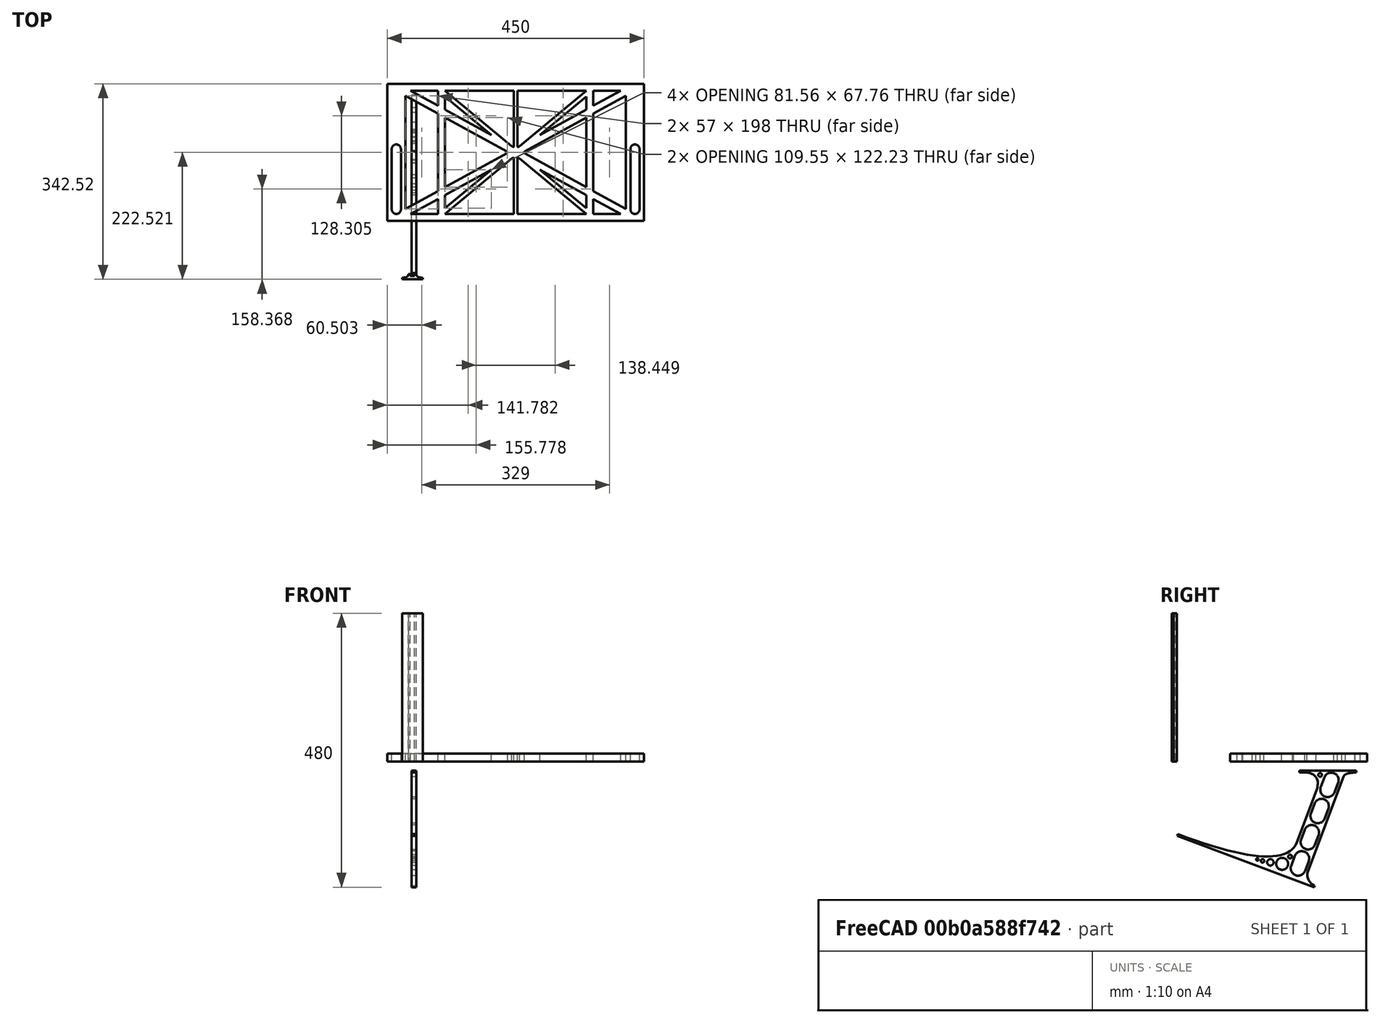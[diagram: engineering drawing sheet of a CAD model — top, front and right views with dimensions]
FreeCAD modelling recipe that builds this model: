
FCSTD DOCUMENT  (FreeCAD 0.19R0.19.2)
Label: laptopStand061
License: All rights reserved
LicenseURL: http://en.wikipedia.org/wiki/All_rights_reserved
objects: Sketcher::SketchObject×3, Part::Extrusion×3
note: 6 computed .brp shape members not serialized (recipe doc carries the construction recipe); baked Part::Feature solids carry a one-line shape summary decoded from their .brp

FEATURE [Sketcher::SketchObject] Sketch
  FullyConstrained = false
  sketch-geometry (101):
    g0: LineSegment StartX=375.073 StartY=115.221 StartZ=0 EndX=318.073 EndY=83.9235 EndZ=0
    g1: LineSegment StartX=-10.9272 StartY=-82.7794 StartZ=0 EndX=46.0728 EndY=-51.4823 EndZ=0
    g2: LineSegment StartX=-1.92719 StartY=124.221 StartZ=0 EndX=46.0728 EndY=97.8651 EndZ=0
    g3: LineSegment StartX=366.073 StartY=-91.7794 StartZ=0 EndX=318.073 EndY=-65.424 EndZ=0
    g4: LineSegment StartX=-10.9272 StartY=105.865 StartZ=0 EndX=-10.9272 EndY=-82.7794 EndZ=0
    g5: LineSegment StartX=375.073 StartY=-82.7794 StartZ=0 EndX=375.073 EndY=115.221 EndZ=0
    g6: LineSegment StartX=-1.92719 StartY=-91.7794 StartZ=0 EndX=46.0728 EndY=-91.7794 EndZ=0
    g7: LineSegment StartX=318.073 StartY=124.221 StartZ=0 EndX=366.073 EndY=124.221 EndZ=0
    g8: LineSegment StartX=306.073 StartY=-81.8102 StartZ=0 EndX=224.513 EndY=-14.0532 EndZ=0
    g9: LineSegment StartX=58.0728 StartY=114.251 StartZ=0 EndX=139.632 EndY=46.4944 EndZ=0
    g10: LineSegment StartX=306.073 StartY=124.221 StartZ=0 EndX=189.124 EndY=27.0628 EndZ=0
    g11: LineSegment StartX=58.0728 StartY=-91.7794 StartZ=0 EndX=175.022 EndY=5.37834 EndZ=0
    g12: LineSegment StartX=58.0728 StartY=-81.8102 StartZ=0 EndX=58.0728 EndY=-58.8351 EndZ=0
    g13: LineSegment StartX=318.073 StartY=124.221 StartZ=0 EndX=318.073 EndY=97.8651 EndZ=0
    g14: LineSegment StartX=306.073 StartY=114.251 StartZ=0 EndX=306.073 EndY=91.2763 EndZ=0
    g15: LineSegment StartX=224.513 StartY=46.4944 StartZ=0 EndX=306.073 EndY=114.251 EndZ=0
    g16: LineSegment StartX=175.022 StartY=27.0628 StartZ=0 EndX=58.0728 EndY=124.221 EndZ=0
    g17: LineSegment StartX=139.632 StartY=-14.0532 StartZ=0 EndX=58.0728 EndY=-81.8102 EndZ=0
    g18: LineSegment StartX=224.513 StartY=46.4944 StartZ=0 EndX=306.073 EndY=91.2763 EndZ=0
    g19: LineSegment StartX=139.632 StartY=-14.0532 StartZ=0 EndX=58.0728 EndY=-58.8351 EndZ=0
    g20: LineSegment StartX=189.124 StartY=5.37834 StartZ=0 EndX=306.073 EndY=-91.7794 EndZ=0
    g21: LineSegment StartX=306.073 StartY=77.3346 StartZ=0 EndX=306.073 EndY=-44.8935 EndZ=0
    g22: LineSegment StartX=318.073 StartY=83.9235 StartZ=0 EndX=318.073 EndY=-51.4823 EndZ=0
    g23: LineSegment StartX=318.073 StartY=97.8651 StartZ=0 EndX=366.073 EndY=124.221 EndZ=0
    g24: LineSegment StartX=306.073 StartY=-58.8351 StartZ=0 EndX=224.513 EndY=-14.0532 EndZ=0
    g25: LineSegment StartX=306.073 StartY=-58.8351 StartZ=0 EndX=306.073 EndY=-81.8102 EndZ=0
    g26: LineSegment StartX=318.073 StartY=-51.4823 StartZ=0 EndX=375.073 EndY=-82.7794 EndZ=0
    g27: LineSegment StartX=318.073 StartY=-65.424 StartZ=0 EndX=318.073 EndY=-91.7794 EndZ=0
    g28: LineSegment StartX=318.073 StartY=-91.7794 StartZ=0 EndX=366.073 EndY=-91.7794 EndZ=0
    g29: LineSegment StartX=58.0728 StartY=-44.8935 StartZ=0 EndX=58.0728 EndY=77.3346 EndZ=0
    g30: LineSegment StartX=46.0728 StartY=-65.424 StartZ=0 EndX=-1.92719 EndY=-91.7794 EndZ=0
    g31: LineSegment StartX=46.0728 StartY=-65.424 StartZ=0 EndX=46.0728 EndY=-91.7794 EndZ=0
    g32: LineSegment StartX=58.0728 StartY=91.2763 StartZ=0 EndX=58.0728 EndY=114.251 EndZ=0
    g33: LineSegment StartX=46.0728 StartY=77.3346 StartZ=0 EndX=46.0728 EndY=-51.4823 EndZ=0
    g34: LineSegment StartX=46.0728 StartY=124.221 StartZ=0 EndX=-1.92719 EndY=124.221 EndZ=0
    g35: LineSegment StartX=58.0728 StartY=91.2763 StartZ=0 EndX=139.632 EndY=46.4944 EndZ=0
    g36: LineSegment StartX=-42.9272 StartY=136.221 StartZ=0 EndX=-42.9272 EndY=-103.779 EndZ=0
    g37: LineSegment StartX=407.073 StartY=136.221 StartZ=0 EndX=407.073 EndY=-103.779 EndZ=0
    g38: LineSegment StartX=179.022 StartY=27.0628 StartZ=0 EndX=179.022 EndY=124.221 EndZ=0
    g39: LineSegment StartX=185.124 StartY=27.0628 StartZ=0 EndX=185.124 EndY=124.221 EndZ=0
    g40: ArcOfCircle CenterX=-26.9272 CenterY=22.1087 CenterZ=0 NormalX=0 NormalY=0 NormalZ=1 AngleXU=0 Radius=8 StartAngle=1e-16 EndAngle=3.14159
    g41: ArcOfCircle CenterX=-26.9272 CenterY=-83.7794 CenterZ=0 NormalX=0 NormalY=0 NormalZ=1 AngleXU=0 Radius=8 StartAngle=3.14159 EndAngle=6.28319
    g42: LineSegment StartX=-34.9272 StartY=22.1087 StartZ=0 EndX=-34.9272 EndY=-83.7794 EndZ=0
    g43: LineSegment StartX=-18.9272 StartY=22.1087 StartZ=0 EndX=-18.9272 EndY=-83.7794 EndZ=0
    g44: LineSegment StartX=185.124 StartY=-91.7794 StartZ=0 EndX=306.073 EndY=-91.7794 EndZ=0
    g45: LineSegment StartX=179.022 StartY=-91.7794 StartZ=0 EndX=58.0728 EndY=-91.7794 EndZ=0
    g46: LineSegment StartX=306.073 StartY=124.221 StartZ=0 EndX=185.124 EndY=124.221 EndZ=0
    g47: LineSegment StartX=179.022 StartY=124.221 StartZ=0 EndX=58.0728 EndY=124.221 EndZ=0
    g48: ArcOfCircle CenterX=391.073 CenterY=22.1087 CenterZ=0 NormalX=0 NormalY=0 NormalZ=1 AngleXU=0 Radius=8 StartAngle=-4.4e-15 EndAngle=3.14159
    g49: LineSegment StartX=399.073 StartY=22.1087 StartZ=0 EndX=399.073 EndY=-83.7794 EndZ=0
    g50: LineSegment StartX=383.073 StartY=22.1087 StartZ=0 EndX=383.073 EndY=-83.7794 EndZ=0
    g51: ArcOfCircle CenterX=391.073 CenterY=-83.7794 CenterZ=0 NormalX=0 NormalY=0 NormalZ=1 AngleXU=0 Radius=8 StartAngle=3.14159 EndAngle=6.28319
    g52: Circle CenterX=175.022 CenterY=27.0628 CenterZ=0 NormalX=0 NormalY=0 NormalZ=1 AngleXU=0 Radius=1
    g53: Circle CenterX=179.022 CenterY=24.8665 CenterZ=0 NormalX=0 NormalY=0 NormalZ=1 AngleXU=0 Radius=1
    g54: Circle CenterX=179.022 CenterY=27.0628 CenterZ=0 NormalX=0 NormalY=0 NormalZ=1 AngleXU=0 Radius=1
    g55: BSplineCurve PolesCount=3 KnotsCount=2 Degree=2 IsPeriodic=0
    g56: GeomPoint X=175.022 Y=27.0628 Z=0
    g57: GeomPoint X=179.022 Y=27.0628 Z=0
    g58: Circle CenterX=189.124 CenterY=27.0628 CenterZ=0 NormalX=0 NormalY=0 NormalZ=1 AngleXU=0 Radius=1
    g59: Circle CenterX=185.124 CenterY=24.8665 CenterZ=0 NormalX=0 NormalY=0 NormalZ=1 AngleXU=0 Radius=1
    g60: Circle CenterX=185.124 CenterY=27.0628 CenterZ=0 NormalX=0 NormalY=0 NormalZ=1 AngleXU=0 Radius=1
    g61: BSplineCurve PolesCount=3 KnotsCount=2 Degree=2 IsPeriodic=0
    g62: GeomPoint X=189.124 Y=27.0628 Z=0
    g63: GeomPoint X=185.124 Y=27.0628 Z=0
    g64: Circle CenterX=175.022 CenterY=5.37834 CenterZ=0 NormalX=0 NormalY=0 NormalZ=1 AngleXU=0 Radius=1
    g65: Circle CenterX=179.022 CenterY=7.57463 CenterZ=0 NormalX=0 NormalY=0 NormalZ=1 AngleXU=0 Radius=1
    g66: Circle CenterX=179.022 CenterY=5.34704 CenterZ=0 NormalX=0 NormalY=0 NormalZ=1 AngleXU=0 Radius=1
    g67: BSplineCurve PolesCount=3 KnotsCount=2 Degree=2 IsPeriodic=0
    g68: GeomPoint X=175.022 Y=5.37834 Z=0
    g69: GeomPoint X=179.022 Y=5.34704 Z=0
    g70: Circle CenterX=189.124 CenterY=5.37834 CenterZ=0 NormalX=0 NormalY=0 NormalZ=1 AngleXU=0 Radius=1
    g71: Circle CenterX=185.124 CenterY=7.57463 CenterZ=0 NormalX=0 NormalY=0 NormalZ=1 AngleXU=0 Radius=1
    g72: Circle CenterX=185.124 CenterY=5.34704 CenterZ=0 NormalX=0 NormalY=0 NormalZ=1 AngleXU=0 Radius=1
    g73: BSplineCurve PolesCount=3 KnotsCount=2 Degree=2 IsPeriodic=0
    g74: GeomPoint X=189.124 Y=5.37834 Z=0
    g75: GeomPoint X=185.124 Y=5.34704 Z=0
    g76: LineSegment StartX=179.022 StartY=5.34704 StartZ=0 EndX=179.022 EndY=-91.7794 EndZ=0
    g77: LineSegment StartX=185.124 StartY=-91.7794 StartZ=0 EndX=185.124 EndY=5.34704 EndZ=0
    g78: Circle CenterX=165.871 CenterY=18.1458 CenterZ=0 NormalX=0 NormalY=0 NormalZ=1 AngleXU=0 Radius=1
    g79: Circle CenterX=169.377 CenterY=16.2206 CenterZ=0 NormalX=0 NormalY=0 NormalZ=1 AngleXU=0 Radius=1
    g80: Circle CenterX=165.871 CenterY=14.2954 CenterZ=0 NormalX=0 NormalY=0 NormalZ=1 AngleXU=0 Radius=1
    g81: BSplineCurve PolesCount=3 KnotsCount=2 Degree=2 IsPeriodic=0
    g82: GeomPoint X=165.871 Y=18.1458 Z=0
    g83: GeomPoint X=165.871 Y=14.2954 Z=0
    g84: Circle CenterX=198.275 CenterY=18.1458 CenterZ=0 NormalX=0 NormalY=0 NormalZ=1 AngleXU=0 Radius=1
    g85: Circle CenterX=194.768 CenterY=16.2206 CenterZ=0 NormalX=0 NormalY=0 NormalZ=1 AngleXU=0 Radius=1
    g86: Circle CenterX=198.275 CenterY=14.2954 CenterZ=0 NormalX=0 NormalY=0 NormalZ=1 AngleXU=0 Radius=1
    g87: BSplineCurve PolesCount=3 KnotsCount=2 Degree=2 IsPeriodic=0
    g88: GeomPoint X=198.275 Y=18.1458 Z=0
    g89: GeomPoint X=198.275 Y=14.2954 Z=0
    g90: LineSegment StartX=165.871 StartY=18.1458 StartZ=0 EndX=58.0728 EndY=77.3346 EndZ=0
    g91: LineSegment StartX=58.0728 StartY=-44.8935 StartZ=0 EndX=165.871 EndY=14.2954 EndZ=0
    g92: LineSegment StartX=198.275 StartY=18.1458 StartZ=0 EndX=306.073 EndY=77.3346 EndZ=0
    g93: LineSegment StartX=198.275 StartY=14.2954 StartZ=0 EndX=306.073 EndY=-44.8935 EndZ=0
    g94: LineSegment StartX=407.073 StartY=-103.779 StartZ=0 EndX=-42.9272 EndY=-103.779 EndZ=0
    g95: LineSegment StartX=407.073 StartY=136.221 StartZ=0 EndX=-42.9272 EndY=136.221 EndZ=0
    g96: LineSegment StartX=-26.9272 StartY=136.221 StartZ=0 EndX=-26.9272 EndY=98.2206 EndZ=0
    g97: LineSegment StartX=46.0728 StartY=77.3346 StartZ=0 EndX=-10.9272 EndY=77.3346 EndZ=0
    g98: LineSegment StartX=46.0728 StartY=105.865 StartZ=0 EndX=-10.9272 EndY=105.865 EndZ=0
    g99: LineSegment StartX=46.0728 StartY=124.221 StartZ=0 EndX=46.0728 EndY=105.865 EndZ=0
    g100: LineSegment StartX=-10.9272 StartY=105.865 StartZ=0 EndX=-8.8296 EndY=116.066 EndZ=0
  constraints (185):
    c: Horizontal(g6)
    c: Horizontal(g7)
    c: Coincident(g35,g9)
    c: Coincident(g15,g18)
    c: Coincident(g19,g17)
    c: Coincident(g24,g8)
    c: Coincident(g15,g14)
    c: Tangent(g14,g21)
    c: Tangent(g13,g22)
    c: Coincident(g18,g14)
    c: Tangent(g18,g23)
    c: Coincident(g0,g22)
    c: Coincident(g25,g8)
    c: Tangent(g3,g24)
    c: Tangent(g21,g25)
    c: Coincident(g22,g26)
    c: Coincident(g27,g3)
    c: Tangent(g22,g27)
    c: Coincident(g17,g12)
    c: Tangent(g12,g29)
    c: Coincident(g19,g12)
    c: Tangent(g19,g30)
    c: Coincident(g31,g30)
    c: Coincident(g1,g33)
    c: Tangent(g29,g32)
    c: Coincident(g9,g32)
    c: Coincident(g35,g32)
    c: Tangent(g2,g35)
    c: Block(g16)
    c: Block(g10)
    c: Block(g13)
    c: Block(g23)
    c: Block(g0)
    c: Block(g26)
    c: Block(g5)
    c: Block(g24)
    c: Block(g25)
    c: Block(g3)
    c: Block(g27)
    c: Block(g15)
    c: Block(g20)
    c: Block(g11)
    c: Block(g19)
    c: Block(g17)
    c: Block(g31)
    c: Block(g30)
    c: Block(g1)
    c: Block(g4)
    c: Block(g2)
    c: Block(g9)
    c: Block(g32)
    c: Block(g21)
    c: Block(g34)
    c: Block(g7)
    c: Block(g28)
    c: Block(g6)
    c: Vertical(g36)
    c: Vertical(g37)
    c: Block(g37)
    c: Block(g36)
    c: Vertical(g38)
    c: Vertical(g39)
    c: Block(g38)
    c: Block(g39)
    c: Tangent(g40,g43) = 1.5708
    c: Tangent(g40,g42) = -1.5708
    c: Tangent(g42,g41) = -1.5708
    c: Tangent(g43,g41) = 1.5708
    c: Vertical(g42)
    c: Equal(g40,g41)
    c: Block(g43)
    c: Block(g42)
    c: Coincident(g44,g20)
    c: Horizontal(g44)
    c: Coincident(g45,g11)
    c: Horizontal(g45)
    c: Coincident(g46,g10)
    c: Coincident(g46,g39)
    c: Horizontal(g46)
    c: Coincident(g47,g38)
    c: Coincident(g47,g16)
    c: Horizontal(g47)
    c: Tangent(g48,g49) = 1.5708
    c: Tangent(g49,g51) = 1.5708
    c: Equal(g48,g51)
    c: Coincident(g50,g48)
    c: Coincident(g50,g51)
    c: Block(g49)
    c: Block(g50)
    c: Coincident(g55,g16)
    c: Weight(g52) = 1
    c: Equal(g52,g53)
    c: Equal(g52,g54)
    c: Coincident(g55,g38)
    c: InternalAlignment(g52,g55)
    c: InternalAlignment(g53,g55)
    c: InternalAlignment(g54,g55)
    c: InternalAlignment(g56,g55)
    c: InternalAlignment(g57,g55)
    c: Coincident(g61,g10)
    c: Weight(g58) = 1
    c: Equal(g58,g59)
    c: Equal(g58,g60)
    c: Coincident(g61,g39)
    c: InternalAlignment(g58,g61)
    c: InternalAlignment(g59,g61)
    c: InternalAlignment(g60,g61)
    c: InternalAlignment(g62,g61)
    c: InternalAlignment(g63,g61)
    c: Block(g61)
    c: Block(g55)
    c: Coincident(g67,g11)
    c: Weight(g64) = 1
    c: Equal(g64,g65)
    c: Equal(g64,g66)
    c: InternalAlignment(g64,g67)
    c: InternalAlignment(g65,g67)
    c: InternalAlignment(g66,g67)
    c: InternalAlignment(g68,g67)
    c: InternalAlignment(g69,g67)
    c: Weight(g70) = 1
    c: Equal(g70,g71)
    c: Equal(g70,g72)
    c: InternalAlignment(g70,g73)
    c: InternalAlignment(g71,g73)
    c: InternalAlignment(g72,g73)
    c: InternalAlignment(g74,g73)
    c: InternalAlignment(g75,g73)
    c: Block(g73)
    c: Block(g67)
    c: Coincident(g76,g67)
    c: Coincident(g76,g45)
    c: Vertical(g76)
    c: Coincident(g77,g44)
    c: Coincident(g77,g73)
    c: Vertical(g77)
    c: Weight(g78) = 1
    c: Equal(g78,g79)
    c: Equal(g78,g80)
    c: InternalAlignment(g78,g81)
    c: InternalAlignment(g79,g81)
    c: InternalAlignment(g80,g81)
    c: InternalAlignment(g82,g81)
    c: InternalAlignment(g83,g81)
    c: Weight(g84) = 1
    c: Equal(g84,g85)
    c: Equal(g84,g86)
    c: InternalAlignment(g84,g87)
    c: InternalAlignment(g85,g87)
    c: InternalAlignment(g86,g87)
    c: InternalAlignment(g88,g87)
    c: InternalAlignment(g89,g87)
    c: Block(g81)
    c: Block(g87)
    c: Coincident(g90,g81)
    c: Coincident(g90,g29)
    c: Coincident(g91,g29)
    c: Coincident(g91,g81)
    c: Coincident(g92,g87)
    c: Coincident(g92,g21)
    c: Coincident(g93,g87)
    c: Coincident(g93,g21)
    c: Block(g29)
    c: Coincident(g94,g37)
    c: Coincident(g94,g36)
    c: Horizontal(g94)
    c: Distance(g94) = 450
    c: Coincident(g95,g37)
    c: Coincident(g95,g36)
    c: Horizontal(g95)
    c: PointOnObject(g96,g95)
    c: Vertical(g96)
    c: Distance(g96) = 38
    c: Horizontal(g97)
    c: PointOnObject(g97,g4)
    c: Coincident(g33,g97)
    c: Horizontal(g98)
    c: Coincident(g99,g34)
    c: Vertical(g99)
    c: Block(g99)
    c: Block(g98)
    c: Block(g97)
    c: Coincident(g4,g98)
    c: Coincident(g100,g4)
    c: Block(g100)
FEATURE [Sketcher::SketchObject] Sketch001
  FullyConstrained = true
  MapMode = 4
  Placement = pos=(0,0,0) rot=(0.57735,0.57735,0.57735;2.0944rad)
  Support = -> [Sketch]
  sketch-geometry (46):
    g0: BSplineCurve PolesCount=3 KnotsCount=2 Degree=2 IsPeriodic=0
    g1: ArcOfCircle CenterX=73.1223 CenterY=-32.291 CenterZ=0 NormalX=0 NormalY=0 NormalZ=1 AngleXU=0 Radius=13 StartAngle=5.92268 EndAngle=9.06428
    g2: ArcOfCircle CenterX=66.7816 CenterY=-49.1439 CenterZ=0 NormalX=0 NormalY=0 NormalZ=1 AngleXU=0 Radius=13 StartAngle=2.78068 EndAngle=5.92131
    g3: ArcOfCircle CenterX=55.9263 CenterY=-78.1807 CenterZ=0 NormalX=0 NormalY=0 NormalZ=1 AngleXU=0 Radius=13 StartAngle=5.92268 EndAngle=9.06428
    g4: ArcOfCircle CenterX=49.5884 CenterY=-95.0342 CenterZ=0 NormalX=0 NormalY=0 NormalZ=1 AngleXU=0 Radius=13 StartAngle=2.78068 EndAngle=5.92131
    g5: ArcOfCircle CenterX=38.7206 CenterY=-124.067 CenterZ=0 NormalX=0 NormalY=0 NormalZ=1 AngleXU=0 Radius=13 StartAngle=5.92268 EndAngle=9.06428
    g6: ArcOfCircle CenterX=32.3875 CenterY=-140.92 CenterZ=0 NormalX=0 NormalY=0 NormalZ=1 AngleXU=0 Radius=13 StartAngle=2.78068 EndAngle=5.92131
    g7: ArcOfCircle CenterX=21.4715 CenterY=-169.934 CenterZ=0 NormalX=0 NormalY=0 NormalZ=1 AngleXU=0 Radius=13 StartAngle=5.92268 EndAngle=9.06428
    g8: ArcOfCircle CenterX=15.1336 CenterY=-186.787 CenterZ=0 NormalX=0 NormalY=0 NormalZ=1 AngleXU=0 Radius=13 StartAngle=2.78068 EndAngle=5.92131
    g9-g12: Circle x4 (B-spline internal-alignment scaffolding for g13; pole/knot coordinates omitted)
    g13: BSplineCurve PolesCount=4 KnotsCount=2 Degree=3 IsPeriodic=0
    g14: GeomPoint X=28.8094 Y=-19.0875 Z=0
    g15: GeomPoint X=47.0443 Y=-50.4712 Z=0
    g16: Circle CenterX=53.5586 CenterY=-23.2695 CenterZ=0 NormalX=0 NormalY=0 NormalZ=1 AngleXU=0 Radius=3.24518
    g17: Circle CenterX=-195.441 CenterY=-127.082 CenterZ=0 NormalX=0 NormalY=0 NormalZ=1 AngleXU=0 Radius=1
    g18: Circle CenterX=-8.24091 CenterY=-197.481 CenterZ=0 NormalX=0 NormalY=0 NormalZ=1 AngleXU=0 Radius=1
    g19: Circle CenterX=12.8789 CenterY=-141.321 CenterZ=0 NormalX=0 NormalY=0 NormalZ=1 AngleXU=0 Radius=1
    g20: BSplineCurve PolesCount=3 KnotsCount=2 Degree=2 IsPeriodic=0
    g21: GeomPoint X=-195.441 Y=-127.082 Z=0
    g22: GeomPoint X=12.8789 Y=-141.321 Z=0
    g23: Circle CenterX=-12.8016 CenterY=-179.036 CenterZ=0 NormalX=0 NormalY=0 NormalZ=1 AngleXU=0 Radius=10.5072
    g24: Circle CenterX=0.933922 CenterY=-166.43 CenterZ=0 NormalX=0 NormalY=0 NormalZ=1 AngleXU=0 Radius=3.26661
    g25: Circle CenterX=-33.5518 CenterY=-176.44 CenterZ=0 NormalX=0 NormalY=0 NormalZ=1 AngleXU=0 Radius=5.64388
    g26: Circle CenterX=-47.2366 CenterY=-173.859 CenterZ=0 NormalX=0 NormalY=0 NormalZ=1 AngleXU=0 Radius=3.01653
    g27: Circle CenterX=-56.2595 CenterY=-171.456 CenterZ=0 NormalX=0 NormalY=0 NormalZ=1 AngleXU=0 Radius=2.12826
    g28: ArcOfCircle CenterX=51.2151 CenterY=-198.473 CenterZ=0 NormalX=0 NormalY=0 NormalZ=1 AngleXU=0 Radius=20 StartAngle=2.78189 EndAngle=4.35269
    g29: LineSegment StartX=32.4951 StartY=-191.433 StartZ=0 EndX=94.6578 EndY=-26.1352 EndZ=0
    g30: LineSegment StartX=43.1192 StartY=-220.001 StartZ=0 EndX=-196.497 EndY=-129.89 EndZ=0
    g31: LineSegment StartX=43.1192 StartY=-220.001 StartZ=0 EndX=44.1752 EndY=-217.193 EndZ=0
    g32: LineSegment StartX=117.223 StartY=-19.0875 StartZ=0 EndX=117.223 EndY=-16.0875 EndZ=0
    g33: LineSegment StartX=117.223 StartY=-16.0875 StartZ=0 EndX=17.2232 EndY=-16.0875 EndZ=0
    g34: LineSegment StartX=17.2232 StartY=-16.0875 StartZ=0 EndX=17.2232 EndY=-19.0875 EndZ=0
    g35: LineSegment StartX=28.8094 StartY=-19.0875 StartZ=0 EndX=17.2232 EndY=-19.0875 EndZ=0
    g36: LineSegment StartX=47.0443 StartY=-50.4712 StartZ=0 EndX=12.8789 EndY=-141.321 EndZ=0
    g37: LineSegment StartX=-195.441 StartY=-127.082 StartZ=0 EndX=-196.497 EndY=-129.89 EndZ=0
    g38: LineSegment StartX=85.2866 StartY=-36.8766 StartZ=0 EndX=78.9396 EndY=-53.7463 EndZ=0
    g39: LineSegment StartX=60.9579 StartY=-27.7053 StartZ=0 EndX=54.6191 EndY=-44.5532 EndZ=0
    g40: LineSegment StartX=68.0907 StartY=-82.7664 StartZ=0 EndX=61.7465 EndY=-99.6365 EndZ=0
    g41: LineSegment StartX=43.7619 StartY=-73.595 StartZ=0 EndX=37.426 EndY=-90.4435 EndZ=0
    g42: LineSegment StartX=50.885 StartY=-128.652 StartZ=0 EndX=44.5456 EndY=-145.522 EndZ=0
    g43: LineSegment StartX=26.5562 StartY=-119.481 StartZ=0 EndX=20.2251 EndY=-136.329 EndZ=0
    g44: LineSegment StartX=9.3071 StartY=-165.349 StartZ=0 EndX=2.97115 EndY=-182.197 EndZ=0
    g45: LineSegment StartX=33.6358 StartY=-174.52 StartZ=0 EndX=27.2917 EndY=-191.39 EndZ=0
  constraints (71):
    c: Block(g0)
    c: Block(g1)
    c: Block(g2)
    c: Block(g4)
    c: Block(g3)
    c: Block(g6)
    c: Block(g5)
    c: Block(g8)
    c: Block(g7)
    c: Weight(g9) = 1
    c: Equal(g9,g10)
    c: Equal(g9,g11)
    c: Equal(g9,g12)
    c: InternalAlignment(g9-g12 -> g13) x4
    c: InternalAlignment(g14,g13)
    c: InternalAlignment(g15,g13)
    c: Block(g16)
    c: Weight(g17) = 1
    c: Equal(g17,g18)
    c: Equal(g17,g19)
    c: InternalAlignment(g17,g20)
    c: InternalAlignment(g18,g20)
    c: InternalAlignment(g19,g20)
    c: InternalAlignment(g21,g20)
    c: InternalAlignment(g22,g20)
    c: Block(g20)
    c: Block(g23)
    c: Block(g24)
    c: Block(g25)
    c: Block(g26)
    c: Block(g27)
    c: Block(g28)
    c: Coincident(g29,g28)
    c: Coincident(g29,g0)
    c: Block(g13)
    c: Coincident(g31,g30)
    c: Coincident(g31,g28)
    c: Block(g31)
    c: Coincident(g32,g0)
    c: Vertical(g32)
    c: Coincident(g33,g32)
    c: Horizontal(g33)
    c: Coincident(g34,g33)
    c: Vertical(g34)
    c: Block(g33)
    c: Coincident(g35,g13)
    c: Coincident(g35,g34)
    c: Horizontal(g35)
    c: Coincident(g36,g13)
    c: Coincident(g36,g20)
    c: Coincident(g37,g20)
    c: Coincident(g37,g30)
    c: Block(g30)
    c: Coincident(g38,g1)
    c: Coincident(g38,g2)
    c: Coincident(g39,g1)
    c: Coincident(g39,g2)
    c: Coincident(g40,g3)
    c: Coincident(g40,g4)
    c: Coincident(g41,g3)
    c: Coincident(g41,g4)
    c: Coincident(g42,g5)
    c: Coincident(g42,g6)
    c: Coincident(g43,g5)
    c: Coincident(g43,g6)
    c: Coincident(g44,g7)
    c: Coincident(g44,g8)
    c: Coincident(g45,g7)
    c: Coincident(g45,g8)
    c: Distance(g30) = 256
    c: Distance(g33) = 100
FEATURE [Part::Extrusion] Extrude002
  Base = -> Sketch001
  Dir = (1,0,0)
  DirMode = 2
  FaceMakerClass = Part::FaceMakerBullseye
  LengthFwd = 8
  LengthRev = 0
  Solid = true
  Symmetric = false
FEATURE [Sketcher::SketchObject] Sketch002
  FullyConstrained = true
  sketch-geometry (20):
    g0: LineSegment StartX=-2.77179 StartY=-200.304 StartZ=0 EndX=5.22821 EndY=-200.304 EndZ=0
    g1: LineSegment StartX=5.22821 StartY=-200.304 StartZ=0 EndX=5.22821 EndY=-197.304 EndZ=0
    g2: LineSegment StartX=-2.77179 StartY=-200.304 StartZ=0 EndX=-2.77179 EndY=-197.304 EndZ=0
    g3: LineSegment StartX=5.22821 StartY=-197.304 StartZ=0 EndX=8.22821 EndY=-197.304 EndZ=0
    g4: LineSegment StartX=-2.77179 StartY=-197.304 StartZ=0 EndX=-5.77179 EndY=-197.304 EndZ=0
    g5: LineSegment StartX=19.2282 StartY=-203.304 StartZ=0 EndX=19.2282 EndY=-206.304 EndZ=0
    g6: LineSegment StartX=-16.7718 StartY=-203.304 StartZ=0 EndX=-16.7718 EndY=-206.304 EndZ=0
    g7: LineSegment StartX=-16.7718 StartY=-206.304 StartZ=0 EndX=19.2282 EndY=-206.304 EndZ=0
    g8: Circle CenterX=-16.7718 CenterY=-203.304 CenterZ=0 NormalX=0 NormalY=0 NormalZ=1 AngleXU=0 Radius=1
    g9: Circle CenterX=-5.77179 CenterY=-203.304 CenterZ=0 NormalX=0 NormalY=0 NormalZ=1 AngleXU=0 Radius=1
    g10: Circle CenterX=-5.77179 CenterY=-197.304 CenterZ=0 NormalX=0 NormalY=0 NormalZ=1 AngleXU=0 Radius=1
    g11: BSplineCurve PolesCount=3 KnotsCount=2 Degree=2 IsPeriodic=0
    g12: GeomPoint X=-16.7718 Y=-203.304 Z=0
    g13: GeomPoint X=-5.77179 Y=-197.304 Z=0
    g14: Circle CenterX=19.2282 CenterY=-203.304 CenterZ=0 NormalX=0 NormalY=0 NormalZ=1 AngleXU=0 Radius=1
    g15: Circle CenterX=8.22821 CenterY=-203.304 CenterZ=0 NormalX=0 NormalY=0 NormalZ=1 AngleXU=0 Radius=1
    g16: Circle CenterX=8.22821 CenterY=-197.304 CenterZ=0 NormalX=0 NormalY=0 NormalZ=1 AngleXU=0 Radius=1
    g17: BSplineCurve PolesCount=3 KnotsCount=2 Degree=2 IsPeriodic=0
    g18: GeomPoint X=19.2282 Y=-203.304 Z=0
    g19: GeomPoint X=8.22821 Y=-197.304 Z=0
  constraints (41):
    c: Horizontal(g0)
    c: Distance(g0) = 8
    c: Coincident(g1,g0)
    c: Vertical(g1)
    c: Distance(g1) = 3
    c: Coincident(g2,g0)
    c: Vertical(g2)
    c: Distance(g2) = 3
    c: Coincident(g3,g1)
    c: Horizontal(g3)
    c: Distance(g3) = 3
    c: Coincident(g4,g2)
    c: Horizontal(g4)
    c: Distance(g4) = 3
    c: Vertical(g5)
    c: Vertical(g6)
    c: Coincident(g7,g6)
    c: Coincident(g7,g5)
    c: Weight(g8) = 1
    c: Equal(g8,g9)
    c: Equal(g8,g10)
    c: Coincident(g11,g4)
    c: InternalAlignment(g8,g11)
    c: InternalAlignment(g9,g11)
    c: InternalAlignment(g10,g11)
    c: InternalAlignment(g12,g11)
    c: InternalAlignment(g13,g11)
    c: Coincident(g17,g5)
    c: Weight(g14) = 1
    c: Equal(g14,g15)
    c: Equal(g14,g16)
    c: Coincident(g17,g3)
    c: InternalAlignment(g14,g17)
    c: InternalAlignment(g15,g17)
    c: InternalAlignment(g16,g17)
    c: InternalAlignment(g18,g17)
    c: InternalAlignment(g19,g17)
    c: Block(g7)
    c: Block(g17)
    c: Block(g11)
    c: Block(g6)
FEATURE [Part::Extrusion] Extrude003
  Base = -> Sketch002
  Dir = (0,0,1)
  DirMode = 2
  FaceMakerClass = Part::FaceMakerBullseye
  LengthFwd = 260
  LengthRev = 0
  Solid = true
  Symmetric = false
FEATURE [Part::Extrusion] Extrude
  Base = -> Sketch
  Dir = (0,0,1)
  DirMode = 2
  FaceMakerClass = Part::FaceMakerBullseye
  LengthFwd = 14
  LengthRev = 0
  Solid = true
  Symmetric = false
